# Revit family: Fuge_BH_Tieppo_Type_p_i_07903
name_source: partatom
category: Generic Models
units: mm (PartAtom-declared; Revit-internal decimal feet)

## family parameters
Always vertical = No
Can host rebar = Yes
Cut with Voids When Loaded = No
Part Type = Normal
Room Calculation Point = No
Round Connector Dimension = Use Diameter
Shared = No
Work Plane-Based = Yes

## types (3) — shared parameters
Default Elevation = 1219 mm
Distance Rebar = 200 mm  [stored 0.656168 ft]
Distance dybel = 490 mm
Model = Tieppo BH
Steel overlap = 20 mm  [stored 0.0656168 ft]
Steel overlap 2 = 80 mm  [stored 0.262467 ft]
Stål 40x8 = Steel, S 235
URL = https://katalog.haucon.no

## per-type parameters (varying)
| type | Distance rebar form | Heigth Rebar | Heigth dybel | Heigth rebar 2 | Hight |
| 100mm | 480 mm  [stored 1.5748 ft] | 90 mm  [stored 0.295276 ft] | 30 mm  [stored 0.0984252 ft] | 60 mm  [stored 0.19685 ft] | 60 mm  [stored 0.19685 ft] |
| 130mm | 490 mm | 121 mm  [stored 0.396982 ft] | 50 mm  [stored 0.164042 ft] | 91 mm  [stored 0.298556 ft] | 90 mm  [stored 0.295276 ft] |
| 180mm | 480 mm  [stored 1.5748 ft] | 165 mm | 80 mm  [stored 0.262467 ft] | 125 mm  [stored 0.410105 ft] | 140 mm |

note: [stored X ft] marks values corroborated as IEEE doubles in the binary element streams (Revit-internal decimal feet)

## geometry (parser evidence)
native form markers: Sweep x20
no freeform markers — native parametric forms only
